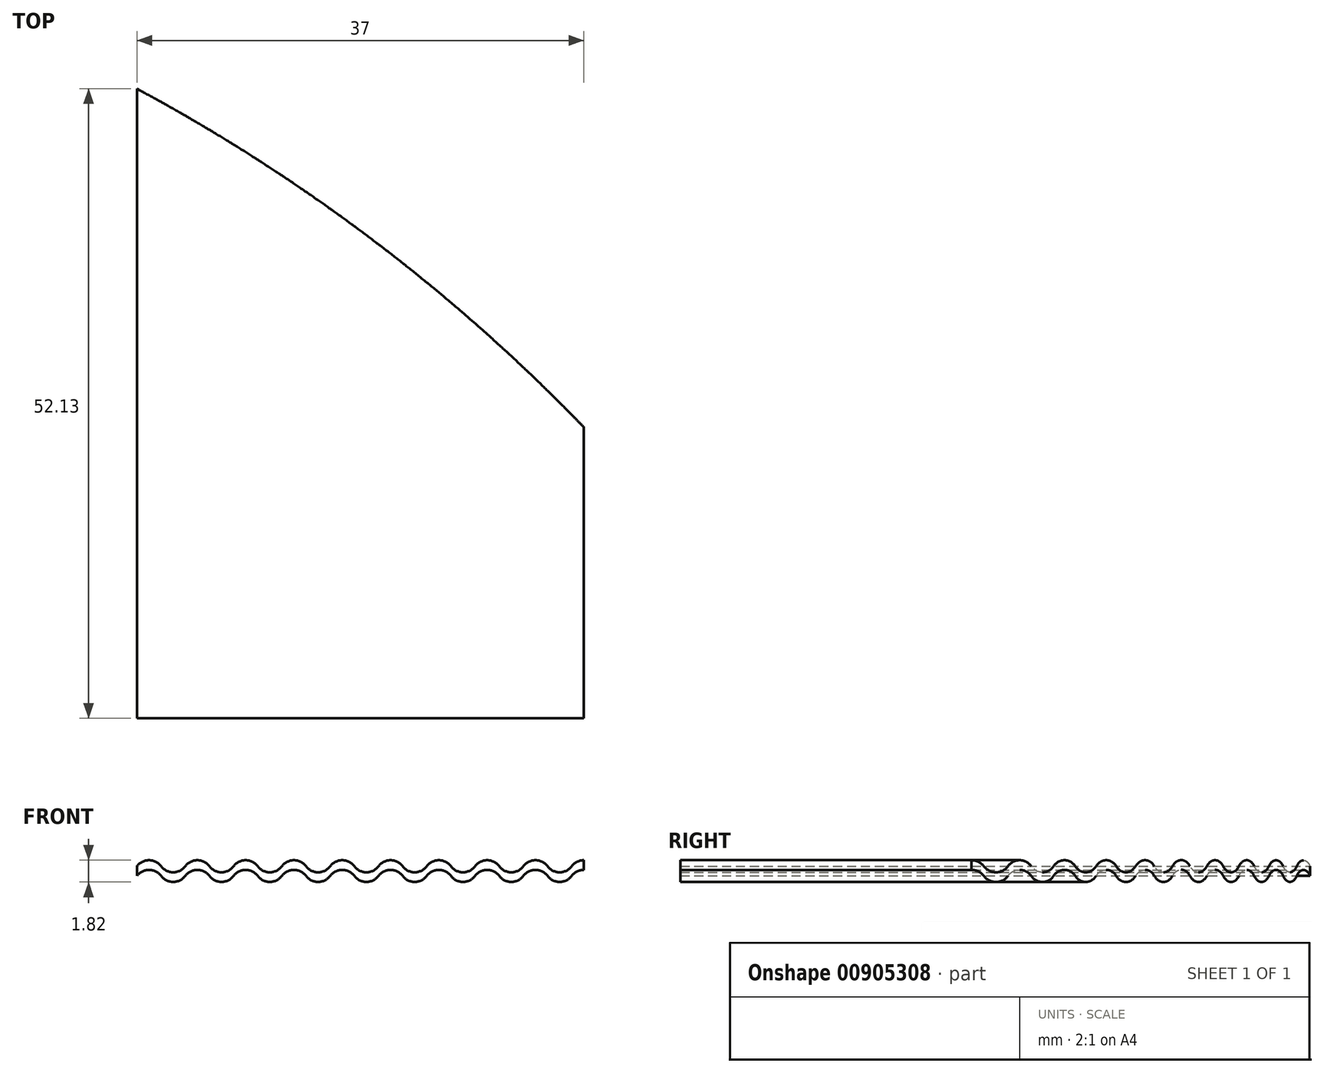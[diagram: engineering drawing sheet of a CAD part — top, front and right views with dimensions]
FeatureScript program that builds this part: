
annotation { "Feature Type Name" : "Feature", "Feature Type Description" : "" }
export const myFeature = defineFeature(function(context is Context, id is Id, definition is map)
    precondition{}
    {
        {
            var Q0;
            Q0=qCreatedBy(makeId("Front.planeOp"),FACE);
            var sketch = newSketch(context, id + "F0", { "sketchPlane" : qUnion([Q0])});
            skArc(sketch, "E0", {"start": v(-19, -0.4) * mm, "mid": v(-20, 0.1) * mm, "end": v(-21, -0.4) * mm});
            skArc(sketch, "E1", {"start": v(-23, -0.4) * mm, "mid": v(-22, -0.9) * mm, "end": v(-21, -0.4) * mm});
            skArc(sketch, "E2", {"start": v(-23, -0.4) * mm, "mid": v(-24, 0.1) * mm, "end": v(-25, -0.4) * mm});
            skArc(sketch, "E3", {"start": v(5, -0.4) * mm, "mid": v(6, -0.9) * mm, "end": v(7, -0.4) * mm});
            skArc(sketch, "E4", {"start": v(9, -0.4) * mm, "mid": v(8, 0.1) * mm, "end": v(7, -0.4) * mm});
            skArc(sketch, "E5", {"start": v(9, -0.4) * mm, "mid": v(10, -0.9) * mm, "end": v(11, -0.4) * mm});
            skArc(sketch, "E6", {"start": v(13, -0.4) * mm, "mid": v(12, 0.1) * mm, "end": v(11, -0.4) * mm});
            skArc(sketch, "E7", {"start": v(13, -0.4) * mm, "mid": v(14, -0.9) * mm, "end": v(15, -0.4) * mm});
            skArc(sketch, "E8", {"start": v(17, -0.4) * mm, "mid": v(16, 0.1) * mm, "end": v(15, -0.4) * mm});
            skArc(sketch, "E9", {"start": v(25, -0.4) * mm, "mid": v(24, 0.1) * mm, "end": v(23, -0.4) * mm});
            skArc(sketch, "E10", {"start": v(21, -0.4) * mm, "mid": v(22, -0.9) * mm, "end": v(23, -0.4) * mm});
            skArc(sketch, "E11", {"start": v(21, -0.4) * mm, "mid": v(20, 0.1) * mm, "end": v(19, -0.4) * mm});
            skArc(sketch, "E12", {"start": v(17, -0.4) * mm, "mid": v(18, -0.9) * mm, "end": v(19, -0.4) * mm});
            skArc(sketch, "E13", {"start": v(5, -0.4) * mm, "mid": v(4, 0.1) * mm, "end": v(3, -0.4) * mm});
            skArc(sketch, "E14", {"start": v(1, -0.4) * mm, "mid": v(2, -0.9) * mm, "end": v(3, -0.4) * mm});
            skArc(sketch, "E15", {"start": v(1, -0.4) * mm, "mid": v(0, 0.1) * mm, "end": v(-1, -0.4) * mm});
            skArc(sketch, "E16", {"start": v(-3, -0.4) * mm, "mid": v(-2, -0.9) * mm, "end": v(-1, -0.4) * mm});
            skArc(sketch, "E17", {"start": v(-3, -0.4) * mm, "mid": v(-4, 0.1) * mm, "end": v(-5, -0.4) * mm});
            skArc(sketch, "E18", {"start": v(-7, -0.4) * mm, "mid": v(-6, -0.9) * mm, "end": v(-5, -0.4) * mm});
            skArc(sketch, "E19", {"start": v(-7, -0.4) * mm, "mid": v(-8, 0.1) * mm, "end": v(-9, -0.4) * mm});
            skArc(sketch, "E20", {"start": v(-11, -0.4) * mm, "mid": v(-10, -0.9) * mm, "end": v(-9, -0.4) * mm});
            skArc(sketch, "E21", {"start": v(-11, -0.4) * mm, "mid": v(-12, 0.1) * mm, "end": v(-13, -0.4) * mm});
            skArc(sketch, "E22", {"start": v(-15, -0.4) * mm, "mid": v(-14, -0.9) * mm, "end": v(-13, -0.4) * mm});
            skArc(sketch, "E23", {"start": v(-15, -0.4) * mm, "mid": v(-16, 0.1) * mm, "end": v(-17, -0.4) * mm});
            skArc(sketch, "E24", {"start": v(-19, -0.4) * mm, "mid": v(-18, -0.9) * mm, "end": v(-17, -0.4) * mm});
            skArc(sketch, "E25", {"start": v(-19, 0.4) * mm, "mid": v(-20, 0.9) * mm, "end": v(-21, 0.4) * mm});
            skArc(sketch, "E26", {"start": v(-23, 0.4) * mm, "mid": v(-22, -0.1) * mm, "end": v(-21, 0.4) * mm});
            skArc(sketch, "E27", {"start": v(-23, 0.4) * mm, "mid": v(-24, 0.9) * mm, "end": v(-25, 0.4) * mm});
            skArc(sketch, "E28", {"start": v(5, 0.4) * mm, "mid": v(6, -0.1) * mm, "end": v(7, 0.4) * mm});
            skArc(sketch, "E29", {"start": v(9, 0.4) * mm, "mid": v(8, 0.9) * mm, "end": v(7, 0.4) * mm});
            skArc(sketch, "E30", {"start": v(9, 0.4) * mm, "mid": v(10, -0.1) * mm, "end": v(11, 0.4) * mm});
            skArc(sketch, "E31", {"start": v(13, 0.4) * mm, "mid": v(12, 0.9) * mm, "end": v(11, 0.4) * mm});
            skArc(sketch, "E32", {"start": v(13, 0.4) * mm, "mid": v(14, -0.1) * mm, "end": v(15, 0.4) * mm});
            skArc(sketch, "E33", {"start": v(17, 0.4) * mm, "mid": v(16, 0.9) * mm, "end": v(15, 0.4) * mm});
            skArc(sketch, "E34", {"start": v(25, 0.4) * mm, "mid": v(24, 0.9) * mm, "end": v(23, 0.4) * mm});
            skArc(sketch, "E35", {"start": v(21, 0.4) * mm, "mid": v(22, -0.1) * mm, "end": v(23, 0.4) * mm});
            skArc(sketch, "E36", {"start": v(21, 0.4) * mm, "mid": v(20, 0.9) * mm, "end": v(19, 0.4) * mm});
            skArc(sketch, "E37", {"start": v(17, 0.4) * mm, "mid": v(18, -0.1) * mm, "end": v(19, 0.4) * mm});
            skArc(sketch, "E38", {"start": v(5, 0.4) * mm, "mid": v(4, 0.9) * mm, "end": v(3, 0.4) * mm});
            skArc(sketch, "E39", {"start": v(1, 0.4) * mm, "mid": v(2, -0.1) * mm, "end": v(3, 0.4) * mm});
            skArc(sketch, "E40", {"start": v(1, 0.4) * mm, "mid": v(0, 0.9) * mm, "end": v(-1, 0.4) * mm});
            skArc(sketch, "E41", {"start": v(-3, 0.4) * mm, "mid": v(-2, -0.1) * mm, "end": v(-1, 0.4) * mm});
            skArc(sketch, "E42", {"start": v(-3, 0.4) * mm, "mid": v(-4, 0.9) * mm, "end": v(-5, 0.4) * mm});
            skArc(sketch, "E43", {"start": v(-7, 0.4) * mm, "mid": v(-6, -0.1) * mm, "end": v(-5, 0.4) * mm});
            skArc(sketch, "E44", {"start": v(-7, 0.4) * mm, "mid": v(-8, 0.9) * mm, "end": v(-9, 0.4) * mm});
            skArc(sketch, "E45", {"start": v(-11, 0.4) * mm, "mid": v(-10, -0.1) * mm, "end": v(-9, 0.4) * mm});
            skArc(sketch, "E46", {"start": v(-11, 0.4) * mm, "mid": v(-12, 0.9) * mm, "end": v(-13, 0.4) * mm});
            skArc(sketch, "E47", {"start": v(-15, 0.4) * mm, "mid": v(-14, -0.1) * mm, "end": v(-13, 0.4) * mm});
            skArc(sketch, "E48", {"start": v(-15, 0.4) * mm, "mid": v(-16, 0.9) * mm, "end": v(-17, 0.4) * mm});
            skArc(sketch, "E49", {"start": v(-19, 0.4) * mm, "mid": v(-18, -0.1) * mm, "end": v(-17, 0.4) * mm});
            skLineSegment(sketch, "E50", {"start": v(-25, 0.4) * mm, "end": v(-25, -0.4) * mm});
            skLineSegment(sketch, "E51", {"start": v(25, 0.4) * mm, "end": v(25, -0.4) * mm});
            skSolve(sketch);
        }
        {
            var Q0;
            Q0=qSketchRegion(id+"F0",true);
            extrude(context, id + "F1", {"entities" : qUnion([Q0]), "depth" : 70 * mm, "offsetDistance" : 25 * mm});
        }
        {
            var Q0;
            Q0=qCreatedBy(makeId("Top.planeOp"),FACE);
            var sketch = newSketch(context, id + "F2", { "sketchPlane" : qUnion([Q0])});
            skLineSegment(sketch, "E52", {"start": v(0, 0) * mm, "end": v(0, -150) * mm, "construction": true});
            skCircle(sketch, "E53", {"center": v(-96, -150) * mm, "radius": 150 * mm});
            skLineSegment(sketch, "E54", {"start": v(-96, -150) * mm, "end": v(54, -150) * mm, "construction": true});
            skLineSegment(sketch, "E55", {"start": v(-96, -150) * mm, "end": v(-24, -150) * mm, "construction": true});
            skLineSegment(sketch, "E56", {"start": v(-24, -150) * mm, "end": v(12, -150) * mm, "construction": true});
            skLineSegment(sketch, "E57", {"start": v(12, -150) * mm, "end": v(12, 0) * mm});
            skLineSegment(sketch, "E58", {"start": v(12, 0) * mm, "end": v(12, -273.38) * mm});
            skSolve(sketch);
        }
        {
            var Q0;
            {var subQ0=sQuery(id+"F2.wireOp",EDGE,"E57");var subQ1=sQuery(id+"F2.wireOp",EDGE,"E53");var subQ2=makeQuery(id+"F2.imprint","INTERSECT",VERTEX,{"derivedFrom":[subQ1,subQ0]});Q0=makeQuery(id+"F2.imprint","IMPRINT",FACE,{"disambiguationData":[TD([[makeQuery(id+"F2.imprint","IMPRINT",EDGE,{"disambiguationData":[TD([[subQ2,-1.0]])],"derivedFrom":subQ1}),1.0]])]});}
            extrude(context, id + "F3", {"entities" : qUnion([Q0]), "operationType" : NewBodyOperationType.INTERSECT, "depth" : 25 * mm, "offsetDistance" : 25 * mm, "hasSecondDirection" : true, "secondDirectionOppositeDirection" : true, "secondDirectionDepth" : 25 * mm});
        }
    });
